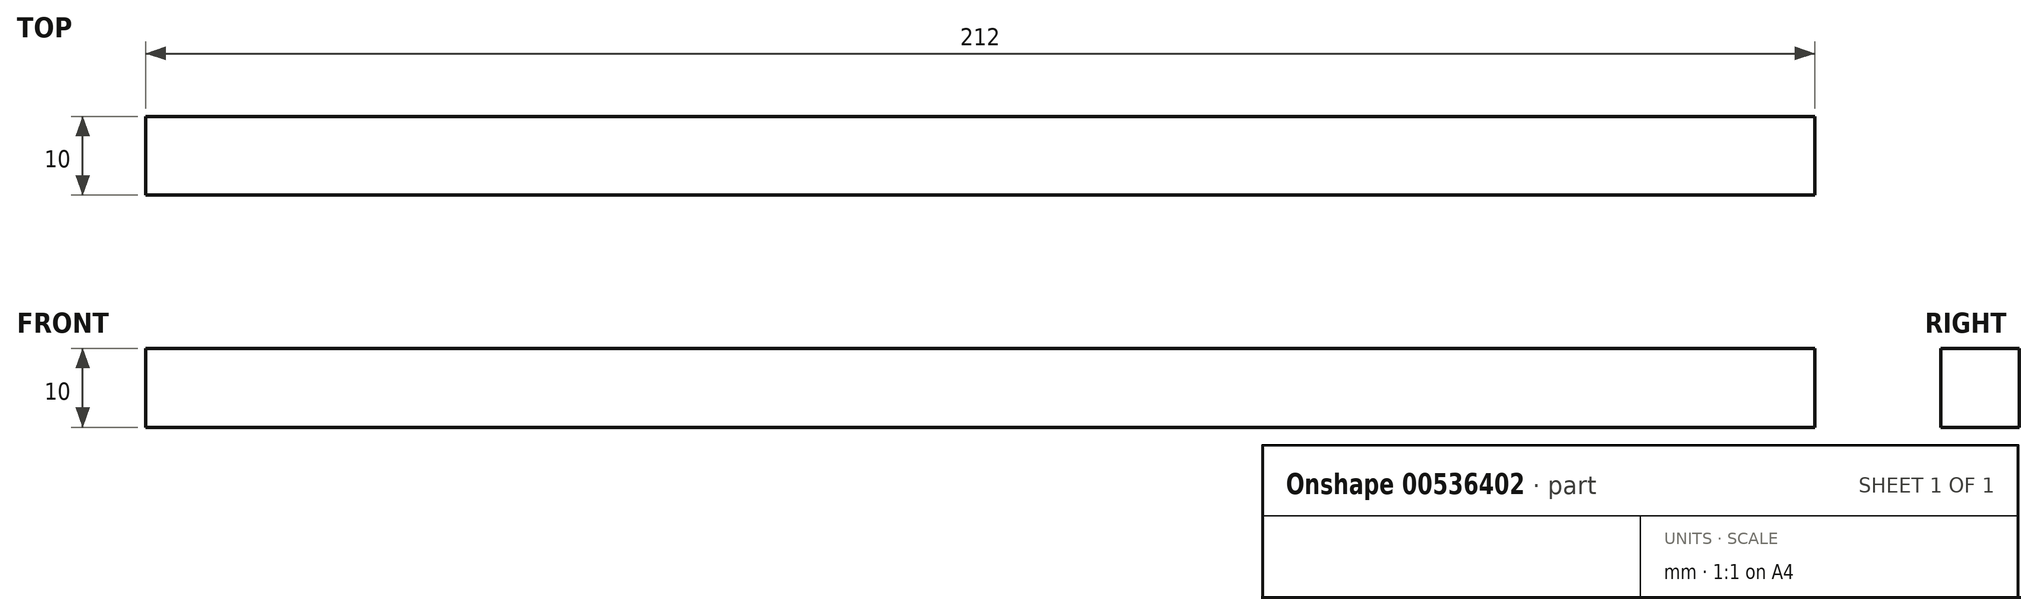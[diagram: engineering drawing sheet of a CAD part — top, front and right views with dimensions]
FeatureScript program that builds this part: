
annotation { "Feature Type Name" : "Feature", "Feature Type Description" : "" }
export const myFeature = defineFeature(function(context is Context, id is Id, definition is map)
    precondition{}
    {
        {
            var Q0;
            Q0=qCreatedBy(makeId("Front.planeOp"),FACE);
            var sketch = newSketch(context, id + "F0", { "sketchPlane" : qUnion([Q0])});
            skLineSegment(sketch, "E0.bottom", {"start": v(106, -5) * mm, "end": v(-106, -5) * mm});
            skLineSegment(sketch, "E0.top", {"start": v(106, 5) * mm, "end": v(-106, 5) * mm});
            skLineSegment(sketch, "E0.left", {"start": v(106, -5) * mm, "end": v(106, 5) * mm});
            skLineSegment(sketch, "E0.right", {"start": v(-106, -5) * mm, "end": v(-106, 5) * mm});
            skPoint(sketch, "E0.middle", {"position": v(0, 0) * mm});
            skSolve(sketch);
        }
        {
            var Q0;
            Q0=qSketchRegion(id+"F0",true);
            extrude(context, id + "F1", {"entities" : qUnion([Q0]), "depth" : 10 * mm});
        }
    });
